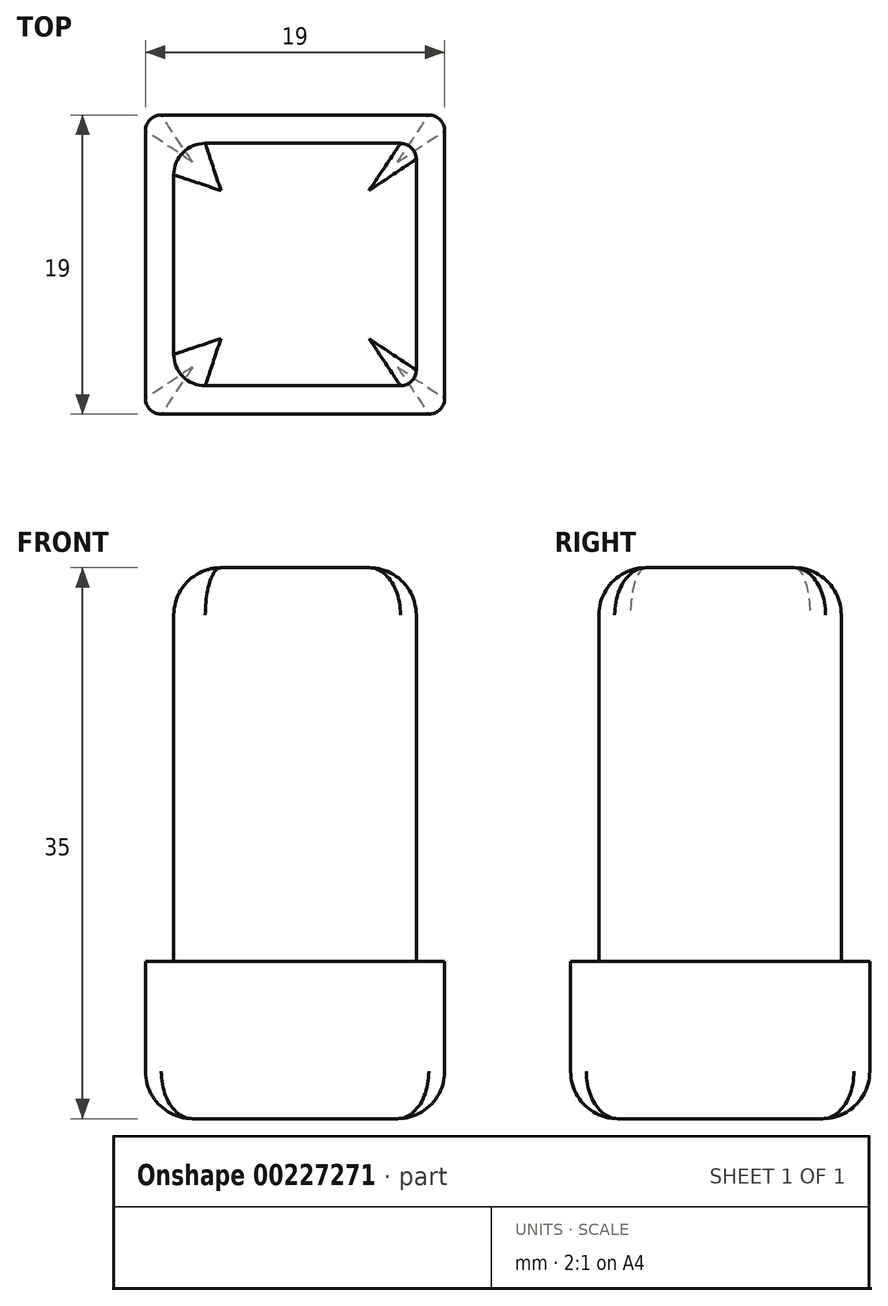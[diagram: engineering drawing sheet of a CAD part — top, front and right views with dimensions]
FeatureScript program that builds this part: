
annotation { "Feature Type Name" : "Feature", "Feature Type Description" : "" }
export const myFeature = defineFeature(function(context is Context, id is Id, definition is map)
    precondition{}
    {
        {
            var Q0;
            Q0=qCreatedBy(makeId("Top.planeOp"),FACE);
            var sketch = newSketch(context, id + "F0", { "sketchPlane" : qUnion([Q0])});
            skLineSegment(sketch, "E0.bottom", {"start": v(0, 0) * mm, "end": v(19, 0) * mm});
            skLineSegment(sketch, "E0.top", {"start": v(0, -19) * mm, "end": v(19, -19) * mm});
            skLineSegment(sketch, "E0.left", {"start": v(0, 0) * mm, "end": v(0, -19) * mm});
            skLineSegment(sketch, "E0.right", {"start": v(19, 0) * mm, "end": v(19, -19) * mm});
            skSolve(sketch);
        }
        {
            var Q0;
            Q0=makeQuery(id+"F0.imprint","IMPRINT",FACE,{"disambiguationData":[TD([[makeQuery(id+"F0.imprint","IMPRINT",EDGE,{"derivedFrom":sQuery(id+"F0.wireOp",EDGE,"E0.bottom")}),-1.0]])]});
            extrude(context, id + "F1", {"entities" : qUnion([Q0]), "depth" : 10 * mm});
        }
        {
            var Q0;
            Q0=makeQuery(id+"F1.opExtrude","CAP_FACE",FACE,{"disambiguationData":[OSD([sQuery(id+"F0.wireOp",EDGE,"E0.bottom"),sQuery(id+"F0.wireOp",EDGE,"E0.top"),sQuery(id+"F0.wireOp",EDGE,"E0.left"),sQuery(id+"F0.wireOp",EDGE,"E0.right")])],"isStart":false});
            var sketch = newSketch(context, id + "F2", { "sketchPlane" : qUnion([Q0])});
            skLineSegment(sketch, "E1.bottom", {"start": v(1.8, -1.8) * mm, "end": v(17.2, -1.8) * mm});
            skLineSegment(sketch, "E1.top", {"start": v(1.8, -17.2) * mm, "end": v(17.2, -17.2) * mm});
            skLineSegment(sketch, "E1.left", {"start": v(1.8, -1.8) * mm, "end": v(1.8, -17.2) * mm});
            skLineSegment(sketch, "E1.right", {"start": v(17.2, -1.8) * mm, "end": v(17.2, -17.2) * mm});
            skSolve(sketch);
        }
        {
            var Q0;
            Q0=makeQuery(id+"F2.imprint","IMPRINT",FACE,{"disambiguationData":[TD([[makeQuery(id+"F2.imprint","IMPRINT",EDGE,{"derivedFrom":sQuery(id+"F2.wireOp",EDGE,"E1.bottom")}),-1.0]])]});
            var sketch = newSketch(context, id + "F3", { "sketchPlane" : qUnion([Q0])});
            skSolve(sketch);
        }
        {
            var Q0;
            Q0 = qSketchRegion(id + "F3", true);
            var Q1;
            Q1=makeQuery(id+"F2.imprint","IMPRINT",FACE,{"disambiguationData":[TD([[makeQuery(id+"F2.imprint","IMPRINT",EDGE,{"derivedFrom":sQuery(id+"F2.wireOp",EDGE,"E1.bottom")}),-1.0]])]});
            extrude(context, id + "F4", {"entities" : qUnion([Q0, Q1]), "operationType" : NewBodyOperationType.ADD, "depth" : 25 * mm});
        }
        {
            var Q0;
            Q0=makeQuery(id+"F1.opExtrude","CAP_EDGE",EDGE,{"disambiguationData":[OSD([sQuery(id+"F0.wireOp",EDGE,"E0.left")])],"isStart":true});
            var Q1;
            Q1=makeQuery(id+"F1.opExtrude","CAP_EDGE",EDGE,{"disambiguationData":[OSD([sQuery(id+"F0.wireOp",EDGE,"E0.top")])],"isStart":true});
            var Q2;
            Q2=makeQuery(id+"F1.opExtrude","CAP_EDGE",EDGE,{"disambiguationData":[OSD([sQuery(id+"F0.wireOp",EDGE,"E0.right")])],"isStart":true});
            var Q3;
            Q3=makeQuery(id+"F1.opExtrude","CAP_EDGE",EDGE,{"disambiguationData":[OSD([sQuery(id+"F0.wireOp",EDGE,"E0.bottom")])],"isStart":true});
            fillet(context, id + "F5", {"entities" : qUnion([Q0, Q1, Q2, Q3]), "radius" : 3 * mm, "tangentPropagation" : true, "allowEdgeOverflow" : false});
        }
        {
            var Q0;
            Q0=makeQuery(id+"F4.opExtrude","SWEPT_EDGE",EDGE,{"disambiguationData":[OSD([sQuery(id+"F2.wireOp",EDGE,"E1.bottom"),sQuery(id+"F2.wireOp",EDGE,"E1.right")])]});
            var Q1;
            Q1=makeQuery(id+"F4.opExtrude","SWEPT_EDGE",EDGE,{"disambiguationData":[OSD([sQuery(id+"F2.wireOp",EDGE,"E1.top"),sQuery(id+"F2.wireOp",EDGE,"E1.right")])]});
            fillet(context, id + "F6", {"entities" : qUnion([Q0, Q1]), "radius" : 1 * mm, "tangentPropagation" : true, "allowEdgeOverflow" : false});
        }
        {
            var Q0;
            Q0=makeQuery(id+"F4.opExtrude","SWEPT_EDGE",EDGE,{"disambiguationData":[OSD([sQuery(id+"F2.wireOp",EDGE,"E1.bottom"),sQuery(id+"F2.wireOp",EDGE,"E1.left")])]});
            var Q1;
            Q1=makeQuery(id+"F4.opExtrude","SWEPT_EDGE",EDGE,{"disambiguationData":[OSD([sQuery(id+"F2.wireOp",EDGE,"E1.top"),sQuery(id+"F2.wireOp",EDGE,"E1.left")])]});
            var Q2;
            {var subQ0=sQuery(id+"F2.wireOp",EDGE,"E1.top");Q2=makeQuery(id+"F6.opFillet","BLEND_EDGE",EDGE,{"blendedFrom":[makeQuery(id+"F4.opExtrude","SWEPT_EDGE",EDGE,{"disambiguationData":[OSD([subQ0,sQuery(id+"F2.wireOp",EDGE,"E1.right")])]}),makeQuery(id+"F4.opExtrude","SWEPT_FACE",FACE,{"disambiguationData":[OSD([subQ0])]})],"blendedInto":[makeQuery(id+"F4.opExtrude","SWEPT_FACE",FACE,{"disambiguationData":[OSD([subQ0])]})]});}
            var Q3;
            {var subQ0=sQuery(id+"F2.wireOp",EDGE,"E1.bottom");Q3=makeQuery(id+"F6.opFillet","BLEND_EDGE",EDGE,{"blendedFrom":[makeQuery(id+"F4.opExtrude","SWEPT_EDGE",EDGE,{"disambiguationData":[OSD([subQ0,sQuery(id+"F2.wireOp",EDGE,"E1.right")])]}),makeQuery(id+"F4.opExtrude","SWEPT_FACE",FACE,{"disambiguationData":[OSD([subQ0])]})],"blendedInto":[makeQuery(id+"F4.opExtrude","SWEPT_FACE",FACE,{"disambiguationData":[OSD([subQ0])]})]});}
            fillet(context, id + "F7", {"entities" : qUnion([Q0, Q1, Q2, Q3]), "radius" : 2 * mm, "tangentPropagation" : true, "allowEdgeOverflow" : false});
        }
        {
            var Q0;
            Q0=makeQuery(id+"F1.opExtrude","SWEPT_EDGE",EDGE,{"disambiguationData":[OSD([sQuery(id+"F0.wireOp",EDGE,"E0.bottom"),sQuery(id+"F0.wireOp",EDGE,"E0.right")])]});
            var Q1;
            Q1=makeQuery(id+"F1.opExtrude","SWEPT_EDGE",EDGE,{"disambiguationData":[OSD([sQuery(id+"F0.wireOp",EDGE,"E0.bottom"),sQuery(id+"F0.wireOp",EDGE,"E0.left")])]});
            var Q2;
            Q2=makeQuery(id+"F1.opExtrude","SWEPT_EDGE",EDGE,{"disambiguationData":[OSD([sQuery(id+"F0.wireOp",EDGE,"E0.top"),sQuery(id+"F0.wireOp",EDGE,"E0.right")])]});
            var Q3;
            Q3=makeQuery(id+"F1.opExtrude","SWEPT_EDGE",EDGE,{"disambiguationData":[OSD([sQuery(id+"F0.wireOp",EDGE,"E0.top"),sQuery(id+"F0.wireOp",EDGE,"E0.left")])]});
            fillet(context, id + "F8", {"entities" : qUnion([Q0, Q1, Q2, Q3]), "radius" : 1 * mm, "tangentPropagation" : true, "allowEdgeOverflow" : false});
        }
        {
            var Q0;
            Q0=makeQuery(id+"F4.opExtrude","CAP_EDGE",EDGE,{"disambiguationData":[OSD([sQuery(id+"F2.wireOp",EDGE,"E1.right")])],"isStart":false});
            fillet(context, id + "F9", {"entities" : qUnion([Q0]), "radius" : 3 * mm, "tangentPropagation" : true, "allowEdgeOverflow" : false});
        }
    });
